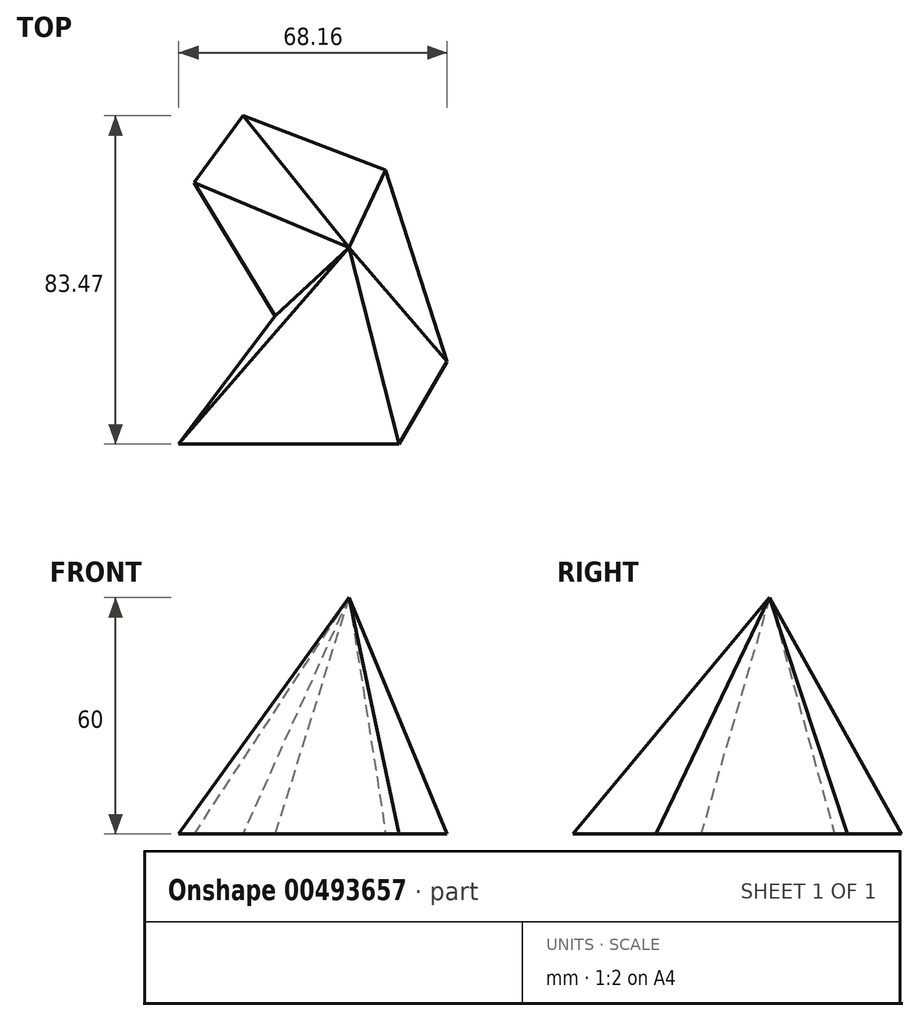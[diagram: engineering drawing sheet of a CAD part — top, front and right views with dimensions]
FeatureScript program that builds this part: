
annotation { "Feature Type Name" : "Feature", "Feature Type Description" : "" }
export const myFeature = defineFeature(function(context is Context, id is Id, definition is map)
    precondition{}
    {
        {
            var Q0;
            Q0=qCreatedBy(makeId("Top.planeOp"),FACE);
            var sketch = newSketch(context, id + "F0", { "sketchPlane" : qUnion([Q0])});
            skLineSegment(sketch, "E0", {"start": v(-43.23, -49.97) * mm, "end": v(12.73, -49.97) * mm});
            skLineSegment(sketch, "E1", {"start": v(12.73, -49.97) * mm, "end": v(24.93, -28.95) * mm});
            skLineSegment(sketch, "E2", {"start": v(24.93, -28.95) * mm, "end": v(9.37, 19.7) * mm});
            skLineSegment(sketch, "E3", {"start": v(9.37, 19.7) * mm, "end": v(-26.9, 33.5) * mm});
            skLineSegment(sketch, "E4", {"start": v(-26.9, 33.5) * mm, "end": v(-39.36, 16.51) * mm});
            skLineSegment(sketch, "E5", {"start": v(-39.36, 16.51) * mm, "end": v(-18.74, -17.43) * mm});
            skLineSegment(sketch, "E6", {"start": v(-18.74, -17.43) * mm, "end": v(-43.23, -49.97) * mm});
            skSolve(sketch);
        }
        {
            var Q0;
            Q0=qCreatedBy(makeId("Top.planeOp"),FACE);
            cPlane(context, id + "F1", {"entities" : qUnion([Q0]), "cplaneType" : CPlaneType.OFFSET, "offset" : 60 * mm, "width" : 150 * mm, "height" : 150 * mm});
        }
        {
            var Q0;
            Q0=qCreatedBy(id+"F1.planeOp",FACE);
            var sketch = newSketch(context, id + "F2", { "sketchPlane" : qUnion([Q0])});
            skPoint(sketch, "E7", {"position": v(0, 0) * mm});
            skSolve(sketch);
        }
        {
            var Q0;
            Q0=sQuery(id+"F2.wireOp",VERTEX,"E7");
            var Q1;
            Q1=makeQuery(id+"F0.imprint","IMPRINT",FACE,{"disambiguationData":[TD([[makeQuery(id+"F0.imprint","IMPRINT",EDGE,{"derivedFrom":sQuery(id+"F0.wireOp",EDGE,"E0")}),1.0]])]});
            loft(context, id + "F3", {"sheetProfilesArray" : [{ "sheetProfileEntities" : qUnion([Q0]) }, { "sheetProfileEntities" : qUnion([Q1]) }]});
        }
    });
